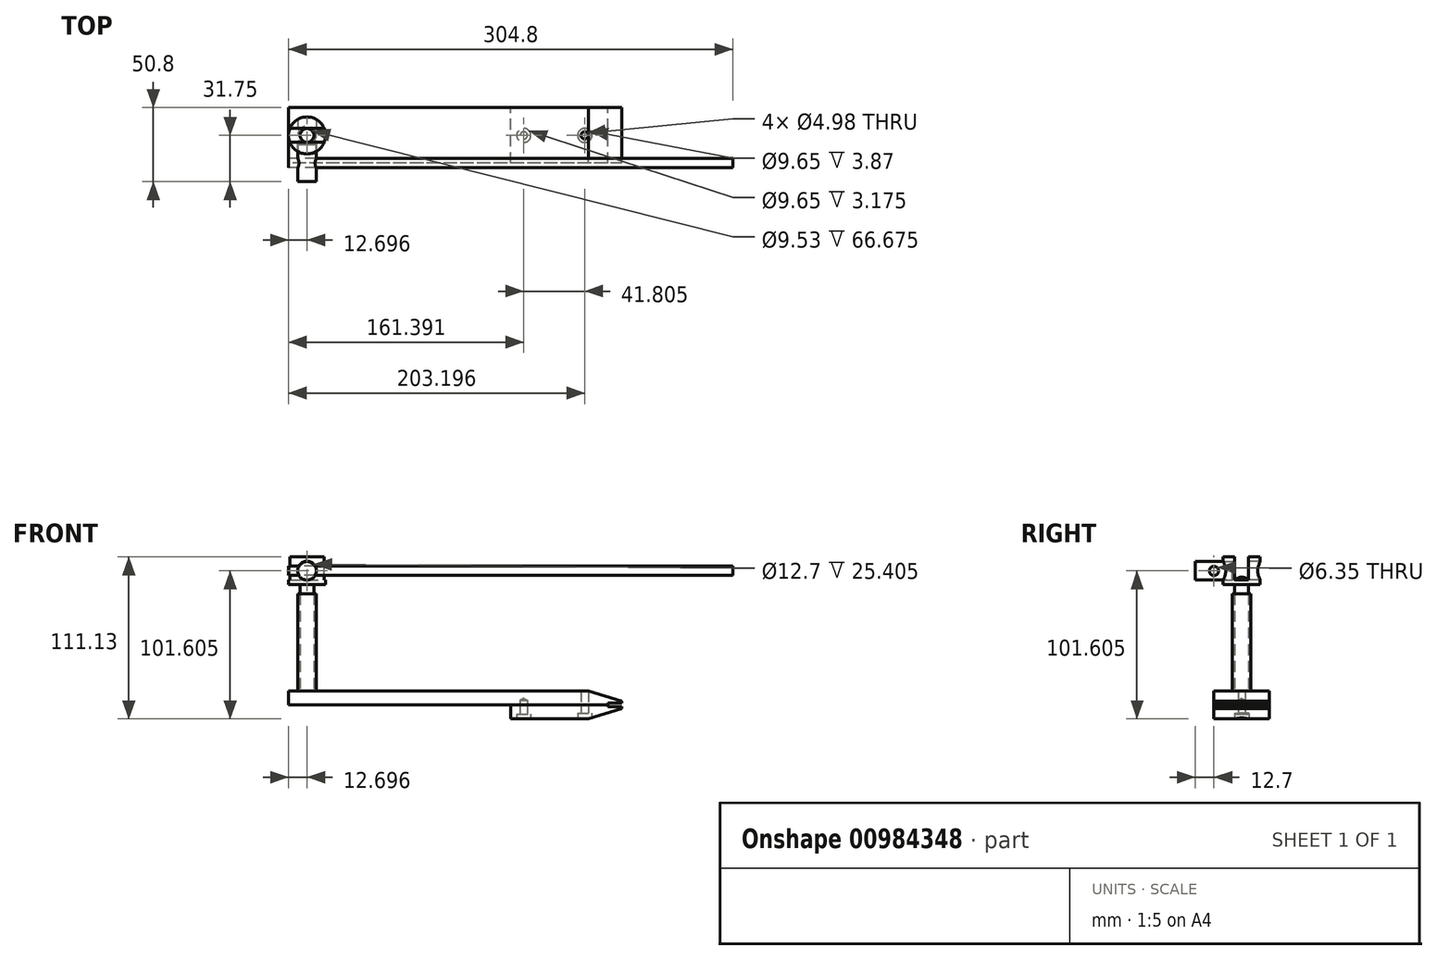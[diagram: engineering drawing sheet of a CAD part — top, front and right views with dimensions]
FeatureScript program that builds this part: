
annotation { "Feature Type Name" : "Feature", "Feature Type Description" : "" }
export const myFeature = defineFeature(function(context is Context, id is Id, definition is map)
    precondition{}
    {
        {
            var Q0;
            Q0=qCreatedBy(makeId("Front.planeOp"),FACE);
            var sketch = newSketch(context, id + "F0", { "sketchPlane" : qUnion([Q0])});
            skLineSegment(sketch, "E0", {"start": v(83.63, 0) * mm, "end": v(-169.47, 0) * mm});
            skLineSegment(sketch, "E1", {"start": v(83.63, 0) * mm, "end": v(-156.77, 133.26) * mm, "construction": true});
            skLineSegment(sketch, "E2", {"start": v(83.63, 0) * mm, "end": v(-156.77, 92.28) * mm, "construction": true});
            skLineSegment(sketch, "E3", {"start": v(-156.77, 112.1) * mm, "end": v(83.63, 0) * mm, "construction": true});
            skLineSegment(sketch, "E4", {"start": v(59.13, 1.27) * mm, "end": v(59.13, 2.54) * mm});
            skLineSegment(sketch, "E5", {"start": v(59.13, 2.54) * mm, "end": v(36.28, 9.53) * mm});
            skLineSegment(sketch, "E6", {"start": v(36.28, 9.53) * mm, "end": v(-169.47, 9.53) * mm});
            skLineSegment(sketch, "E7", {"start": v(-169.47, 9.53) * mm, "end": v(-169.47, 0) * mm});
            skLineSegment(sketch, "E8", {"start": v(59.13, 1.27) * mm, "end": v(49.6, 1.27) * mm});
            skPoint(sketch, "E8.endSnap0", {"position": v(49.6, 4.76) * mm});
            skLineSegment(sketch, "E9", {"start": v(49.6, 1.27) * mm, "end": v(49.6, 0) * mm});
            skPoint(sketch, "E10.orphan", {"position": v(59.13, 0) * mm});
            skLineSegment(sketch, "E11.MirrorCS", {"start": v(49.6, -1.27) * mm, "end": v(49.6, 0) * mm});
            skLineSegment(sketch, "E12.MirrorCS", {"start": v(59.13, -1.27) * mm, "end": v(49.6, -1.27) * mm});
            skLineSegment(sketch, "E13.MirrorCS", {"start": v(59.13, -1.27) * mm, "end": v(59.13, -2.54) * mm});
            skLineSegment(sketch, "E14.MirrorCS", {"start": v(59.13, -2.54) * mm, "end": v(36.28, -9.53) * mm});
            skLineSegment(sketch, "E15.MirrorCS", {"start": v(36.28, -9.53) * mm, "end": v(-169.47, -9.53) * mm});
            skLineSegment(sketch, "E16", {"start": v(-17.07, -9.53) * mm, "end": v(-17.07, 0) * mm});
            skLineSegment(sketch, "E17", {"start": v(-156.77, 9.53) * mm, "end": v(-156.77, 133.26) * mm, "construction": true});
            skSolve(sketch);
        }
        {
            var Q0;
            Q0=makeQuery(id+"F0.imprint","IMPRINT",FACE,{"disambiguationData":[TD([[makeQuery(id+"F0.imprint","IMPRINT",EDGE,{"derivedFrom":sQuery(id+"F0.wireOp",EDGE,"E4")}),1.0]])]});
            extrude(context, id + "F1", {"entities" : qUnion([Q0]), "endBound" : BoundingType.SYMMETRIC, "depth" : 38.1 * mm, "offsetDistance" : 25.4 * mm});
        }
        {
            var Q0;
            {var subQ0=sQuery(id+"F0.wireOp",EDGE,"E11.MirrorCS");Q0=makeQuery(id+"F0.imprint","IMPRINT",FACE,{"disambiguationData":[TD([[makeQuery(id+"F0.imprint","IMPRINT",EDGE,{"derivedFrom":subQ0}),1.0]])]});}
            extrude(context, id + "F2", {"entities" : qUnion([Q0]), "endBound" : BoundingType.SYMMETRIC, "depth" : 38.1 * mm, "offsetDistance" : 25.4 * mm});
        }
        {
            var Q0;
            Q0=makeQuery(id+"F2.opExtrude","SWEPT_FACE",FACE,{"disambiguationData":[OSD([sQuery(id+"F0.wireOp",EDGE,"E15.MirrorCS")])]});
            var sketch = newSketch(context, id + "F3", { "sketchPlane" : qUnion([Q0])});
            skCircle(sketch, "E18", {"center": v(33.73, 0) * mm, "radius": 2.02 * mm});
            skCircle(sketch, "E19", {"center": v(-8.08, 0) * mm, "radius": 2.68 * mm});
            skSolve(sketch);
        }
        {
            var Q0;
            Q0=sQuery(id+"F3.wireOp",VERTEX,"E18.center");
            var Q1;
            Q1=makeQuery(id+"F1.opExtrude","SWEPT_BODY",BODY,{"disambiguationData":[OSD([sQuery(id+"F0.wireOp",EDGE,"E0"),sQuery(id+"F0.wireOp",EDGE,"E4"),sQuery(id+"F0.wireOp",EDGE,"E5"),sQuery(id+"F0.wireOp",EDGE,"E6"),sQuery(id+"F0.wireOp",EDGE,"E7"),sQuery(id+"F0.wireOp",EDGE,"E8"),sQuery(id+"F0.wireOp",EDGE,"E9")])]});
            var Q2;
            Q2=makeQuery(id+"F2.opExtrude","SWEPT_BODY",BODY,{"disambiguationData":[OSD([sQuery(id+"F0.wireOp",EDGE,"E0"),sQuery(id+"F0.wireOp",EDGE,"E11.MirrorCS"),sQuery(id+"F0.wireOp",EDGE,"E12.MirrorCS"),sQuery(id+"F0.wireOp",EDGE,"E13.MirrorCS"),sQuery(id+"F0.wireOp",EDGE,"E14.MirrorCS"),sQuery(id+"F0.wireOp",EDGE,"E15.MirrorCS"),sQuery(id+"F0.wireOp",EDGE,"E16")])]});
            hole(context, id + "F4", {"style" : HoleStyle.C_BORE, "endStyle" : HoleEndStyle.THROUGH, "holeDiameter" : 4.98 * mm, "cBoreDiameter" : 9.65 * mm, "cBoreDepth" : 3.17 * mm, "majorDiameter" : 6.35 * mm, "isTappedThrough" : true, "tappedDepth" : 12.7 * mm, "tapClearance" : 3, "locations" : qUnion([Q0]), "scope" : qUnion([Q1, Q2])});
        }
        {
            var Q0;
            Q0=sQuery(id+"F3.wireOp",VERTEX,"E19.center");
            var Q1;
            Q1=makeQuery(id+"F1.opExtrude","SWEPT_BODY",BODY,{"disambiguationData":[OSD([sQuery(id+"F0.wireOp",EDGE,"E0"),sQuery(id+"F0.wireOp",EDGE,"E4"),sQuery(id+"F0.wireOp",EDGE,"E5"),sQuery(id+"F0.wireOp",EDGE,"E6"),sQuery(id+"F0.wireOp",EDGE,"E7"),sQuery(id+"F0.wireOp",EDGE,"E8"),sQuery(id+"F0.wireOp",EDGE,"E9")])]});
            var Q2;
            Q2=makeQuery(id+"F2.opExtrude","SWEPT_BODY",BODY,{"disambiguationData":[OSD([sQuery(id+"F0.wireOp",EDGE,"E0"),sQuery(id+"F0.wireOp",EDGE,"E11.MirrorCS"),sQuery(id+"F0.wireOp",EDGE,"E12.MirrorCS"),sQuery(id+"F0.wireOp",EDGE,"E13.MirrorCS"),sQuery(id+"F0.wireOp",EDGE,"E14.MirrorCS"),sQuery(id+"F0.wireOp",EDGE,"E15.MirrorCS"),sQuery(id+"F0.wireOp",EDGE,"E16")])]});
            hole(context, id + "F5", {"style" : HoleStyle.C_BORE, "endStyle" : HoleEndStyle.BLIND, "holeDiameter" : 4.98 * mm, "cBoreDiameter" : 9.65 * mm, "cBoreDepth" : 3.17 * mm, "majorDiameter" : 6.35 * mm, "holeDepth" : 12.7 * mm, "isTappedThrough" : true, "tappedDepth" : 12.7 * mm, "tapClearance" : 3, "locations" : qUnion([Q0]), "scope" : qUnion([Q1, Q2])});
        }
        {
            var Q0;
            Q0=makeQuery(id+"F1.opExtrude","SWEPT_FACE",FACE,{"disambiguationData":[OSD([sQuery(id+"F0.wireOp",EDGE,"E6")])]});
            var sketch = newSketch(context, id + "F6", { "sketchPlane" : qUnion([Q0])});
            skCircle(sketch, "E20", {"center": v(-156.77, 0) * mm, "radius": 4.76 * mm});
            skCircle(sketch, "E21", {"center": v(-156.77, 0) * mm, "radius": 6.35 * mm});
            skSolve(sketch);
        }
        {
            var Q0;
            Q0=makeQuery(id+"F6.imprint","IMPRINT",FACE,{"disambiguationData":[TD([[makeQuery(id+"F6.imprint","IMPRINT",EDGE,{"derivedFrom":sQuery(id+"F6.wireOp",EDGE,"E20")}),-1.0]])]});
            extrude(context, id + "F7", {"entities" : qUnion([Q0]), "operationType" : NewBodyOperationType.ADD, "depth" : 66.67 * mm, "offsetDistance" : 25.4 * mm});
        }
        {
            var Q0;
            Q0=makeQuery(id+"F6.imprint","IMPRINT",FACE,{"disambiguationData":[TD([[makeQuery(id+"F6.imprint","IMPRINT",EDGE,{"derivedFrom":sQuery(id+"F6.wireOp",EDGE,"E20")}),1.0]])]});
            extrude(context, id + "F8", {"entities" : qUnion([Q0]), "depth" : 82.55 * mm, "offsetDistance" : 25.4 * mm});
        }
        {
            var Q0;
            Q0=makeQuery(id+"F8.opExtrude","CAP_FACE",FACE,{"disambiguationData":[OSD([sQuery(id+"F6.wireOp",EDGE,"E20")])],"isStart":false});
            var sketch = newSketch(context, id + "F9", { "sketchPlane" : qUnion([Q0])});
            skCircle(sketch, "E22", {"center": v(-156.77, 0) * mm, "radius": 12.7 * mm});
            skLineSegment(sketch, "E23", {"start": v(-169.47, 0) * mm, "end": v(-144.07, 0) * mm, "construction": true});
            skSolve(sketch);
        }
        {
            var Q0;
            Q0=makeQuery(id+"F9.imprint","IMPRINT",FACE,{"disambiguationData":[TD([[makeQuery(id+"F9.imprint","IMPRINT",EDGE,{"derivedFrom":sQuery(id+"F9.wireOp",EDGE,"E22")}),1.0]])]});
            extrude(context, id + "F10", {"entities" : qUnion([Q0]), "operationType" : NewBodyOperationType.ADD, "endBound" : BoundingType.SYMMETRIC, "depth" : 19.05 * mm, "offsetDistance" : 25.4 * mm});
        }
        {
            var Q0;
            Q0=sQuery(id+"F0.wireOp",VERTEX,"E2.end");
            var Q1;
            Q1=makeQuery(id+"F10.opExtrude","SWEPT_BODY",BODY,{"disambiguationData":[OSD([sQuery(id+"F6.wireOp",EDGE,"E20"),sQuery(id+"F9.wireOp",EDGE,"E22")])]});
            var Q2;
            Q2=makeQuery(id+"F8.opExtrude","SWEPT_BODY",BODY,{"disambiguationData":[OSD([sQuery(id+"F6.wireOp",EDGE,"E20")])]});
            hole(context, id + "F11", {"style" : HoleStyle.SIMPLE, "endStyle" : HoleEndStyle.THROUGH, "oppositeDirection" : true, "holeDiameter" : 12.7 * mm, "majorDiameter" : 6.35 * mm, "isTappedThrough" : true, "tappedDepth" : 12.7 * mm, "tapClearance" : 3, "locations" : qUnion([Q0]), "scope" : qUnion([Q1, Q2])});
        }
        {
            var Q0;
            Q0=makeQuery(id+"F10.opExtrude","CAP_FACE",FACE,{"disambiguationData":[OSD([sQuery(id+"F6.wireOp",EDGE,"E20"),sQuery(id+"F9.wireOp",EDGE,"E22")])],"isStart":false});
            var sketch = newSketch(context, id + "F12", { "sketchPlane" : qUnion([Q0])});
            skLineSegment(sketch, "E24", {"start": v(-169.47, 0) * mm, "end": v(-144.07, 0) * mm, "construction": true});
            skLineSegment(sketch, "E25", {"start": v(-168.55, 4.76) * mm, "end": v(-145, 4.76) * mm});
            skLineSegment(sketch, "E26.MirrorCS", {"start": v(-168.55, -4.76) * mm, "end": v(-145, -4.76) * mm});
            skCircle(sketch, "E27", {"center": v(-156.77, 0) * mm, "radius": 12.7 * mm});
            skSolve(sketch);
        }
        {
            var Q0;
            {var subQ0=sQuery(id+"F12.wireOp",EDGE,"E27");var subQ1=sQuery(id+"F12.wireOp",EDGE,"E25");var subQ2=makeQuery(id+"F12.imprint","INTERSECT",VERTEX,{"disambiguationData":[OD(0.0)],"derivedFrom":[subQ1,subQ0]});Q0=makeQuery(id+"F12.imprint","IMPRINT",FACE,{"disambiguationData":[TD([[makeQuery(id+"F12.imprint","IMPRINT",EDGE,{"disambiguationData":[TD([[subQ2,-1.0]])],"derivedFrom":subQ1}),-1.0]])]});}
            var Q1;
            {var subQ0=sQuery(id+"F12.wireOp",EDGE,"E27");var subQ1=sQuery(id+"F12.wireOp",EDGE,"E25");var subQ2=makeQuery(id+"F12.imprint","INTERSECT",VERTEX,{"disambiguationData":[OD(1.0)],"derivedFrom":[subQ1,subQ0]});Q1=makeQuery(id+"F12.imprint","IMPRINT",FACE,{"disambiguationData":[TD([[makeQuery(id+"F12.imprint","IMPRINT",EDGE,{"disambiguationData":[TD([[subQ2,1.0]])],"derivedFrom":subQ1}),-1.0]])]});}
            extrude(context, id + "F13", {"entities" : qUnion([Q0, Q1]), "operationType" : NewBodyOperationType.REMOVE, "oppositeDirection" : true, "depth" : 15.88 * mm, "offsetDistance" : 25.4 * mm});
        }
        {
            var Q0;
            Q0=makeQuery(id+"F1.opExtrude","CAP_FACE",FACE,{"disambiguationData":[OSD([sQuery(id+"F0.wireOp",EDGE,"E0"),sQuery(id+"F0.wireOp",EDGE,"E4"),sQuery(id+"F0.wireOp",EDGE,"E5"),sQuery(id+"F0.wireOp",EDGE,"E6"),sQuery(id+"F0.wireOp",EDGE,"E7"),sQuery(id+"F0.wireOp",EDGE,"E8"),sQuery(id+"F0.wireOp",EDGE,"E9")])],"isStart":false});
            var sketch = newSketch(context, id + "F14", { "sketchPlane" : qUnion([Q0])});
            skCircle(sketch, "E28", {"center": v(-156.77, 92.08) * mm, "radius": 2.8 * mm});
            skCircle(sketch, "E29", {"center": v(-156.77, 92.08) * mm, "radius": 6.35 * mm});
            skSolve(sketch);
        }
        {
            var Q0;
            Q0=sQuery(id+"F14.wireOp",VERTEX,"E28.center");
            var Q1;
            Q1=makeQuery(id+"F10.opExtrude","SWEPT_BODY",BODY,{"disambiguationData":[OSD([sQuery(id+"F6.wireOp",EDGE,"E20"),sQuery(id+"F9.wireOp",EDGE,"E22")])]});
            var Q2;
            Q2=makeQuery(id+"F8.opExtrude","SWEPT_BODY",BODY,{"disambiguationData":[OSD([sQuery(id+"F6.wireOp",EDGE,"E20")])]});
            hole(context, id + "F15", {"style" : HoleStyle.SIMPLE, "endStyle" : HoleEndStyle.THROUGH, "holeDiameter" : 12.7 * mm, "majorDiameter" : 6.35 * mm, "isTappedThrough" : true, "tappedDepth" : 12.7 * mm, "tapClearance" : 3, "locations" : qUnion([Q0]), "scope" : qUnion([Q1, Q2])});
        }
        {
            var Q0;
            Q0=makeQuery(id+"F14.imprint","IMPRINT",FACE,{"disambiguationData":[TD([[makeQuery(id+"F14.imprint","IMPRINT",EDGE,{"derivedFrom":sQuery(id+"F14.wireOp",EDGE,"E29")}),1.0]])]});
            var Q1;
            {var subQ0=sQuery(id+"F14.wireOp",EDGE,"E28");var subQ1=makeQuery(id+"F11.hole-0.boolean.opBoolean","INTERSECT",EDGE,{"derivedFrom":[makeQuery(id+"F8.opExtrude","CAP_FACE",FACE,{"disambiguationData":[OSD([sQuery(id+"F6.wireOp",EDGE,"E20")])],"isStart":false}),makeQuery(id+"F11.hole-0.opRevolve","SWEPT_FACE",FACE,{"disambiguationData":[OSD([sQuery(id+"F11.hole-0.sketch.wireOp",EDGE,"core_line_3")])]})]});var subQ2=makeQuery(id+"F14.imprint","INTERSECT",VERTEX,{"disambiguationData":[OD(0.0)],"derivedFrom":[subQ1,subQ0]});Q1=makeQuery(id+"F14.imprint","IMPRINT",FACE,{"disambiguationData":[TD([[makeQuery(id+"F14.imprint","IMPRINT",EDGE,{"disambiguationData":[TD([[subQ2,1.0]])],"derivedFrom":subQ0}),1.0]])]});}
            var Q2;
            {var subQ0=sQuery(id+"F14.wireOp",EDGE,"E28");var subQ1=makeQuery(id+"F11.hole-0.boolean.opBoolean","INTERSECT",EDGE,{"derivedFrom":[makeQuery(id+"F8.opExtrude","CAP_FACE",FACE,{"disambiguationData":[OSD([sQuery(id+"F6.wireOp",EDGE,"E20")])],"isStart":false}),makeQuery(id+"F11.hole-0.opRevolve","SWEPT_FACE",FACE,{"disambiguationData":[OSD([sQuery(id+"F11.hole-0.sketch.wireOp",EDGE,"core_line_3")])]})]});var subQ2=makeQuery(id+"F14.imprint","INTERSECT",VERTEX,{"disambiguationData":[OD(0.0)],"derivedFrom":[subQ1,subQ0]});Q2=makeQuery(id+"F14.imprint","IMPRINT",FACE,{"disambiguationData":[TD([[makeQuery(id+"F14.imprint","IMPRINT",EDGE,{"disambiguationData":[TD([[subQ2,-1.0]])],"derivedFrom":subQ0}),1.0]])]});}
            var Q3;
            {var subQ4=sQuery(id+"F11.hole-0.sketch.wireOp",EDGE,"core_line_3");Q3=makeQuery(id+"F14.imprint","IMPRINT",FACE,{"disambiguationData":[TD([[makeQuery(id+"F14.imprint","IMPRINT",EDGE,{"derivedFrom":makeQuery(id+"F11.hole-0.boolean.opBoolean","COPY",EDGE,{"derivedFrom":makeQuery(id+"F11.hole-0.opRevolve","SWEPT_EDGE",EDGE,{"disambiguationData":[OSD([sQuery(id+"F11.hole-0.sketch.wireOp",EDGE,"core_line_2"),subQ4])]})})}),-1.0]])]});}
            extrude(context, id + "F16", {"entities" : qUnion([Q0, Q1, Q2, Q3]), "endBound" : BoundingType.SYMMETRIC, "depth" : 25.4 * mm, "offsetDistance" : 25.4 * mm});
        }
        {
            var Q0;
            Q0=makeQuery(id+"F1.opExtrude","SWEPT_FACE",FACE,{"disambiguationData":[OSD([sQuery(id+"F0.wireOp",EDGE,"E7")])]});
            var sketch = newSketch(context, id + "F17", { "sketchPlane" : qUnion([Q0])});
            skCircle(sketch, "E30", {"center": v(19.05, 92.08) * mm, "radius": 3.18 * mm});
            skSolve(sketch);
        }
        {
            var Q0;
            Q0=sQuery(id+"F17.wireOp",VERTEX,"E30.center");
            var Q1;
            Q1=makeQuery(id+"F16.opExtrude","SWEPT_BODY",BODY,{"disambiguationData":[OSD([sQuery(id+"F14.wireOp",EDGE,"E29")])]});
            hole(context, id + "F18", {"style" : HoleStyle.SIMPLE, "endStyle" : HoleEndStyle.THROUGH, "holeDiameter" : 6.35 * mm, "majorDiameter" : 6.35 * mm, "isTappedThrough" : true, "tappedDepth" : 12.7 * mm, "tapClearance" : 3, "locations" : qUnion([Q0]), "scope" : qUnion([Q1])});
        }
        {
            var Q0;
            Q0=makeQuery(id+"F17.imprint","IMPRINT",FACE,{"disambiguationData":[TD([[makeQuery(id+"F17.imprint","IMPRINT",EDGE,{"derivedFrom":sQuery(id+"F17.wireOp",EDGE,"E30")}),1.0]])]});
            extrude(context, id + "F19", {"entities" : qUnion([Q0]), "oppositeDirection" : true, "depth" : 304.8 * mm, "offsetDistance" : 25.4 * mm});
        }
    });
